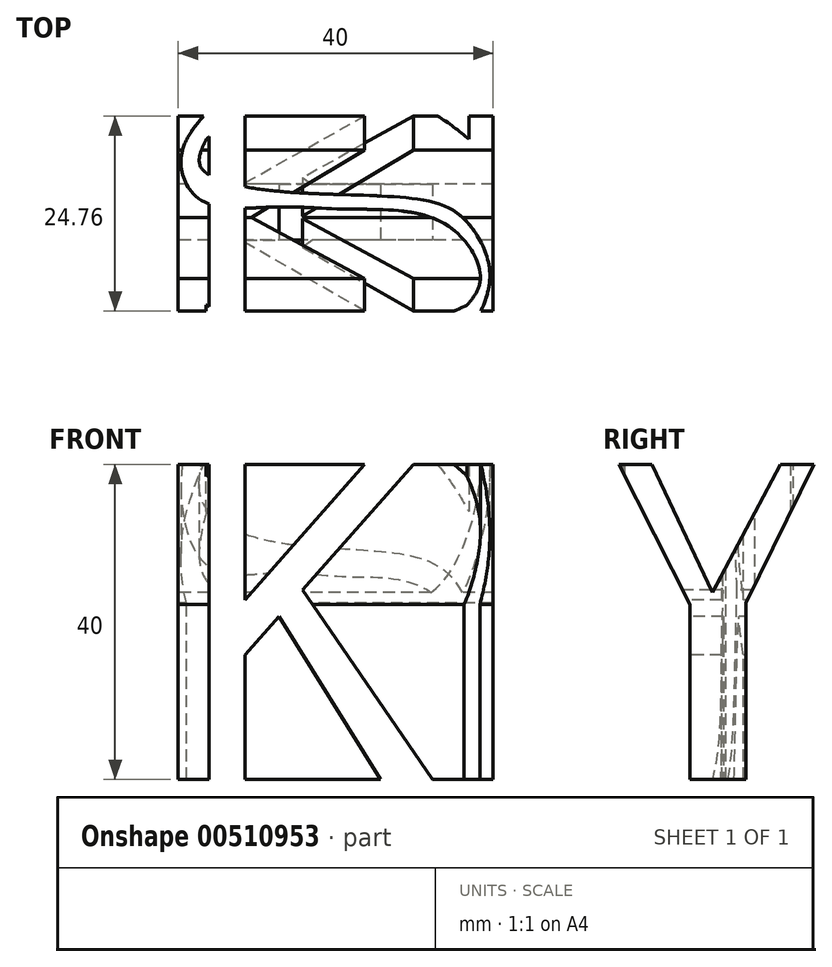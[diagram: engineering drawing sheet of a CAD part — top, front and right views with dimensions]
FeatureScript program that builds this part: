
annotation { "Feature Type Name" : "Feature", "Feature Type Description" : "" }
export const myFeature = defineFeature(function(context is Context, id is Id, definition is map)
    precondition{}
    {
        {
            var Q0;
            Q0=qCreatedBy(makeId("Front.planeOp"),FACE);
            var sketch = newSketch(context, id + "F0", { "sketchPlane" : qUnion([Q0])});
            skLineSegment(sketch, "E0.bottom", {"start": v(-20.43, 24.35) * mm, "end": v(19.57, 24.35) * mm});
            skLineSegment(sketch, "E0.top", {"start": v(-20.43, -15.65) * mm, "end": v(19.57, -15.65) * mm});
            skLineSegment(sketch, "E0.left", {"start": v(-20.43, 24.35) * mm, "end": v(-20.43, -15.65) * mm});
            skLineSegment(sketch, "E0.right", {"start": v(19.57, 24.35) * mm, "end": v(19.57, -15.65) * mm});
            skLineSegment(sketch, "E1", {"start": v(-16.5, 24.35) * mm, "end": v(-16.5, -15.65) * mm});
            skLineSegment(sketch, "E2", {"start": v(-11.94, -15.65) * mm, "end": v(-11.94, 24.35) * mm});
            skLineSegment(sketch, "E3", {"start": v(-11.94, 7.17) * mm, "end": v(3.24, 24.35) * mm});
            skLineSegment(sketch, "E4", {"start": v(9.44, 24.35) * mm, "end": v(-11.94, 0.15) * mm});
            skLineSegment(sketch, "E5", {"start": v(-7.6, 5.05) * mm, "end": v(5.26, -15.65) * mm});
            skLineSegment(sketch, "E6", {"start": v(-4.62, 8.43) * mm, "end": v(11.84, -15.65) * mm});
            skSolve(sketch);
        }
        {
            var Q0;
            {var subQ0=sQuery(id+"F0.wireOp",EDGE,"E0.left");Q0=makeQuery(id+"F0.imprint","IMPRINT",FACE,{"disambiguationData":[TD([[makeQuery(id+"F0.imprint","IMPRINT",EDGE,{"derivedFrom":subQ0}),1.0]])]});}
            var Q1;
            {var subQ3=sQuery(id+"F0.wireOp",EDGE,"E3");Q1=makeQuery(id+"F0.imprint","IMPRINT",FACE,{"disambiguationData":[TD([[makeQuery(id+"F0.imprint","IMPRINT",EDGE,{"derivedFrom":subQ3}),1.0]])]});}
            var Q2;
            {var subQ3=sQuery(id+"F0.wireOp",EDGE,"E5");Q2=makeQuery(id+"F0.imprint","IMPRINT",FACE,{"disambiguationData":[TD([[makeQuery(id+"F0.imprint","IMPRINT",EDGE,{"derivedFrom":subQ3}),-1.0]])]});}
            var Q3;
            {var subQ4=sQuery(id+"F0.wireOp",EDGE,"E0.right");Q3=makeQuery(id+"F0.imprint","IMPRINT",FACE,{"disambiguationData":[TD([[makeQuery(id+"F0.imprint","IMPRINT",EDGE,{"derivedFrom":subQ4}),-1.0]])]});}
            extrude(context, id + "F1", {"entities" : qUnion([Q0, Q1, Q2, Q3]), "oppositeDirection" : true, "depth" : 40 * mm});
        }
        {
            var Q0;
            {var subQ0=sQuery(id+"F0.wireOp",EDGE,"E0.bottom");Q0=makeQuery(id+"F1.opExtrude","SWEPT_FACE",FACE,{"disambiguationData":[OSD([subQ0]),TDD([makeQuery(id+"F0.imprint","IMPRINT",EDGE,{"disambiguationData":[TD([[makeQuery(id+"F0.imprint","INTERSECT",VERTEX,{"derivedFrom":[subQ0,sQuery(id+"F0.wireOp",EDGE,"E2")]}),-1.0]])],"derivedFrom":subQ0})])]});}
            var sketch = newSketch(context, id + "F2", { "sketchPlane" : qUnion([Q0])});
            skLineSegment(sketch, "E7", {"start": v(16.49, 33.81) * mm, "end": v(16.49, 30) * mm});
            skLineSegment(sketch, "E8", {"start": v(-16.87, 8.94) * mm, "end": v(-16.87, 5.13) * mm});
            skArc(sketch, "E9", {"start": v(16.49, 33.81) * mm, "mid": v(8.9, 38.67) * mm, "end": v(0, 40) * mm});
            skArc(sketch, "E10", {"start": v(0, 40) * mm, "mid": v(-8.79, 38.4) * mm, "end": v(-16.44, 33.81) * mm});
            skArc(sketch, "E11", {"start": v(-16.87, 5.13) * mm, "mid": v(-8.76, 1.5) * mm, "end": v(0, 0) * mm});
            skArc(sketch, "E12", {"start": v(0, 0) * mm, "mid": v(8.66, 1.23) * mm, "end": v(16.49, 5.13) * mm});
            skArc(sketch, "E13", {"start": v(-16.87, 8.94) * mm, "mid": v(-0.3, 5.12) * mm, "end": v(16.27, 8.94) * mm});
            skArc(sketch, "E14", {"start": v(16.49, 30) * mm, "mid": v(-0.2, 36.43) * mm, "end": v(-16.87, 30) * mm});
            skFitSpline(sketch, "E15", {"points": [v(-16.87, 30) * mm, v(-17.57, 26.47) * mm, v(-7.5, 23.37) * mm, v(11.2, 22.18) * mm, v(16.55, 19.15) * mm, v(19.16, 12.68) * mm, v(16.49, 5.13) * mm], "startDerivative": vector(-16.92, -34.84) * mm, "endDerivative": vector(-24.78, -46.21) * mm});
            skFitSpline(sketch, "E16", {"points": [v(16.27, 8.94) * mm, v(17.96, 12.47) * mm, v(13.25, 19.36) * mm, v(0.8, 21.12) * mm, v(-7.93, 21.4) * mm, v(-17.5, 22.25) * mm, v(-20.03, 27.95) * mm, v(-16.44, 33.81) * mm], "startDerivative": vector(25.2, 30.5) * mm, "endDerivative": vector(36.71, 41.02) * mm});
            skSolve(sketch);
        }
        {
            var Q0;
            Q0 = qSketchRegion(id + "F2", true);
            extrude(context, id + "F3", {"entities" : qUnion([Q0]), "operationType" : NewBodyOperationType.REMOVE, "oppositeDirection" : true, "depth" : 40 * mm});
        }
        {
            var Q0;
            Q0=makeQuery(id+"F1.opExtrude","SWEPT_FACE",FACE,{"disambiguationData":[OSD([sQuery(id+"F0.wireOp",EDGE,"E0.left")])]});
            var sketch = newSketch(context, id + "F4", { "sketchPlane" : qUnion([Q0])});
            skLineSegment(sketch, "E17", {"start": v(-32.94, 24.35) * mm, "end": v(-24.3, 6.78) * mm});
            skLineSegment(sketch, "E18", {"start": v(-24.3, 6.78) * mm, "end": v(-24.3, -15.65) * mm});
            skLineSegment(sketch, "E19", {"start": v(-24.3, -15.65) * mm, "end": v(-17.19, -15.65) * mm});
            skLineSegment(sketch, "E20", {"start": v(-17.19, -15.65) * mm, "end": v(-17.19, 6.57) * mm});
            skLineSegment(sketch, "E21", {"start": v(-17.19, 6.57) * mm, "end": v(-8.18, 24.35) * mm});
            skLineSegment(sketch, "E22", {"start": v(-8.18, 24.35) * mm, "end": v(-12.33, 24.35) * mm});
            skLineSegment(sketch, "E23", {"start": v(-12.33, 24.35) * mm, "end": v(-20.07, 8.11) * mm});
            skLineSegment(sketch, "E24", {"start": v(-20.07, 8.11) * mm, "end": v(-28.65, 24.35) * mm});
            skLineSegment(sketch, "E25", {"start": v(-28.65, 24.35) * mm, "end": v(-32.94, 24.35) * mm});
            skSolve(sketch);
        }
        {
            var Q0;
            {var subQ3=sQuery(id+"F4.wireOp",EDGE,"E17");Q0=makeQuery(id+"F4.imprint","IMPRINT",FACE,{"disambiguationData":[TD([[makeQuery(id+"F4.imprint","IMPRINT",EDGE,{"derivedFrom":subQ3}),-1.0]])]});}
            var Q1;
            {var subQ4=sQuery(id+"F4.wireOp",EDGE,"E20");Q1=makeQuery(id+"F4.imprint","IMPRINT",FACE,{"disambiguationData":[TD([[makeQuery(id+"F4.imprint","IMPRINT",EDGE,{"derivedFrom":subQ4}),-1.0]])]});}
            var Q2;
            {var subQ0=sQuery(id+"F4.wireOp",EDGE,"E23");Q2=makeQuery(id+"F4.imprint","IMPRINT",FACE,{"disambiguationData":[TD([[makeQuery(id+"F4.imprint","IMPRINT",EDGE,{"derivedFrom":subQ0}),-1.0]])]});}
            extrude(context, id + "F5", {"entities" : qUnion([Q0, Q1, Q2]), "operationType" : NewBodyOperationType.REMOVE, "oppositeDirection" : true, "depth" : 40 * mm});
        }
    });
